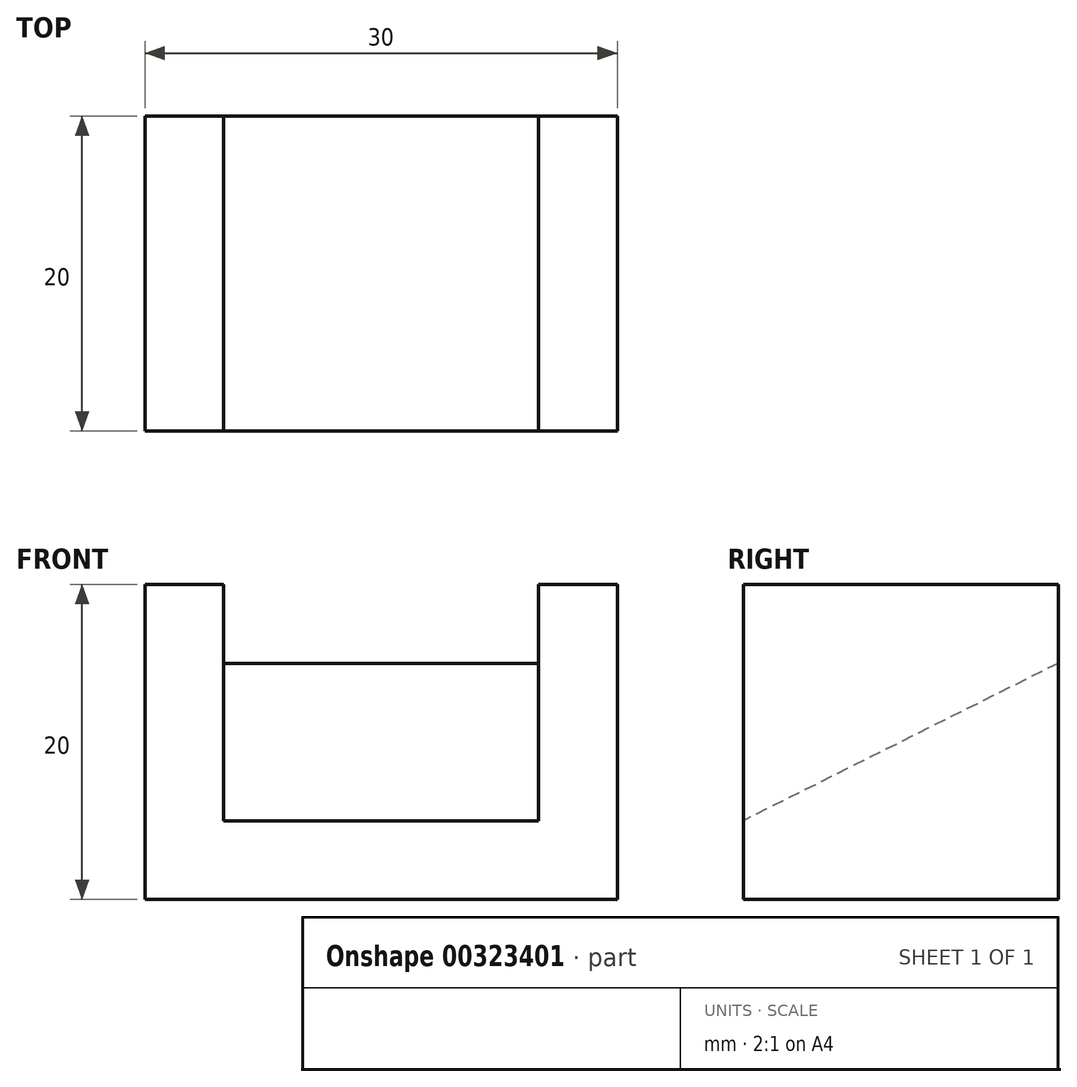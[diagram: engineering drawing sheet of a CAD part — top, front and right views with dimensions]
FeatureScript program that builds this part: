
annotation { "Feature Type Name" : "Feature", "Feature Type Description" : "" }
export const myFeature = defineFeature(function(context is Context, id is Id, definition is map)
    precondition{}
    {
        {
            var Q0;
            Q0=qCreatedBy(makeId("Front.planeOp"),FACE);
            var sketch = newSketch(context, id + "F0", { "sketchPlane" : qUnion([Q0])});
            skLineSegment(sketch, "E0.bottom", {"start": v(0, 0) * mm, "end": v(5, 0) * mm});
            skLineSegment(sketch, "E0.top", {"start": v(0, 20) * mm, "end": v(5, 20) * mm});
            skLineSegment(sketch, "E0.left", {"start": v(0, 0) * mm, "end": v(0, 20) * mm});
            skLineSegment(sketch, "E0.right", {"start": v(5, 0) * mm, "end": v(5, 20) * mm});
            skSolve(sketch);
        }
        {
            var Q0;
            Q0 = qSketchRegion(id + "F0", true);
            extrude(context, id + "F1", {"entities" : qUnion([Q0]), "depth" : 20 * mm});
        }
        {
            var Q0;
            Q0=makeQuery(id+"F1.opExtrude","SWEPT_FACE",FACE,{"disambiguationData":[OSD([sQuery(id+"F0.wireOp",EDGE,"E0.right")])]});
            var sketch = newSketch(context, id + "F2", { "sketchPlane" : qUnion([Q0])});
            skLineSegment(sketch, "E1", {"start": v(0, 15) * mm, "end": v(-20, 5) * mm});
            skLineSegment(sketch, "E2", {"start": v(-20, 5) * mm, "end": v(0, 5) * mm});
            skLineSegment(sketch, "E3", {"start": v(0, 5) * mm, "end": v(0, 15) * mm});
            skSolve(sketch);
        }
        {
            var Q0;
            Q0 = qSketchRegion(id + "F2", true);
            extrude(context, id + "F3", {"entities" : qUnion([Q0]), "operationType" : NewBodyOperationType.ADD, "depth" : 20 * mm});
        }
        {
            var Q0;
            Q0=makeQuery(id+"F3.boolean.opBoolean","MERGE",FACE,{"derivedFrom":[makeQuery(id+"F1.opExtrude","CAP_FACE",FACE,{"disambiguationData":[OSD([sQuery(id+"F0.wireOp",EDGE,"E0.bottom"),sQuery(id+"F0.wireOp",EDGE,"E0.top"),sQuery(id+"F0.wireOp",EDGE,"E0.left"),sQuery(id+"F0.wireOp",EDGE,"E0.right")])],"isStart":true}),makeQuery(id+"F3.opExtrude","SWEPT_FACE",FACE,{"disambiguationData":[OSD([sQuery(id+"F2.wireOp",EDGE,"E3")])]})]});
            var sketch = newSketch(context, id + "F4", { "sketchPlane" : qUnion([Q0])});
            skPoint(sketch, "E4.oppositeSnap0", {"position": v(-2.5, 20) * mm});
            skLineSegment(sketch, "E4.bottom", {"start": v(-25, 0) * mm, "end": v(-30, 0) * mm});
            skLineSegment(sketch, "E4.top", {"start": v(-25, 20) * mm, "end": v(-30, 20) * mm});
            skLineSegment(sketch, "E4.left", {"start": v(-25, 0) * mm, "end": v(-25, 20) * mm});
            skLineSegment(sketch, "E4.right", {"start": v(-30, 0) * mm, "end": v(-30, 20) * mm});
            skSolve(sketch);
        }
        {
            var Q0;
            Q0 = qSketchRegion(id + "F4", true);
            extrude(context, id + "F5", {"entities" : qUnion([Q0]), "operationType" : NewBodyOperationType.ADD, "oppositeDirection" : true, "depth" : 20 * mm});
        }
        {
            var Q0;
            Q0=makeQuery(id+"F5.boolean.opBoolean","MERGE",FACE,{"derivedFrom":[makeQuery(id+"F3.boolean.opBoolean","MERGE",FACE,{"derivedFrom":[makeQuery(id+"F1.opExtrude","CAP_FACE",FACE,{"disambiguationData":[OSD([sQuery(id+"F0.wireOp",EDGE,"E0.bottom"),sQuery(id+"F0.wireOp",EDGE,"E0.top"),sQuery(id+"F0.wireOp",EDGE,"E0.left"),sQuery(id+"F0.wireOp",EDGE,"E0.right")])],"isStart":true}),makeQuery(id+"F3.opExtrude","SWEPT_FACE",FACE,{"disambiguationData":[OSD([sQuery(id+"F2.wireOp",EDGE,"E3")])]})]}),makeQuery(id+"F5.opExtrude","CAP_FACE",FACE,{"disambiguationData":[OSD([sQuery(id+"F4.wireOp",EDGE,"E4.bottom"),sQuery(id+"F4.wireOp",EDGE,"E4.top"),sQuery(id+"F4.wireOp",EDGE,"E4.left"),sQuery(id+"F4.wireOp",EDGE,"E4.right")])],"isStart":true})]});
            var sketch = newSketch(context, id + "F6", { "sketchPlane" : qUnion([Q0])});
            skLineSegment(sketch, "E5.bottom", {"start": v(-25, 0) * mm, "end": v(-5, 0) * mm});
            skLineSegment(sketch, "E5.top", {"start": v(-25, 5) * mm, "end": v(-5, 5) * mm});
            skLineSegment(sketch, "E5.left", {"start": v(-25, 0) * mm, "end": v(-25, 5) * mm});
            skLineSegment(sketch, "E5.right", {"start": v(-5, 0) * mm, "end": v(-5, 5) * mm});
            skSolve(sketch);
        }
        {
            var Q0;
            Q0 = qSketchRegion(id + "F6", true);
            extrude(context, id + "F7", {"entities" : qUnion([Q0]), "operationType" : NewBodyOperationType.ADD, "oppositeDirection" : true, "depth" : 20 * mm});
        }
    });
